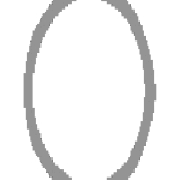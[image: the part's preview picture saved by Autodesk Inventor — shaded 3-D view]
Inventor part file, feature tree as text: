
AUTODESK INVENTOR PART (.ipt)
format: ipt  version: 2021 (Build 250183000, 183)  size: 110,080 bytes
history: native  units: in
note: dims shown in document units (in); Inventor stores cm internally (conversion verified against a paired STEP export)
features: other x4, sketch x3, plane x1
ambient origin geometry x8: Origin, YZ Plane, XZ Plane, XY Plane, X Axis, Y Axis, Z Axis, Center Point
bodies: Solid1 (feature_tree), Body (feature_tree)
feature tree (8):
  other  "Driven Length"
  other  "Frame Generator"
  other  "Start Plane"
  other  "End Plane"
  sketch  "Sketch"  dims[d2=21.1542in d4=-0.0in d5=21.1542in d6=0.12in d7=0.0in d8=90.0deg d9=21.1542in]
  sketch  "Sketch2"  dims[d0=1.0in]
  plane  "Work Plane3"
  sketch  "Sketch3"  dims[d1=0.065in]
